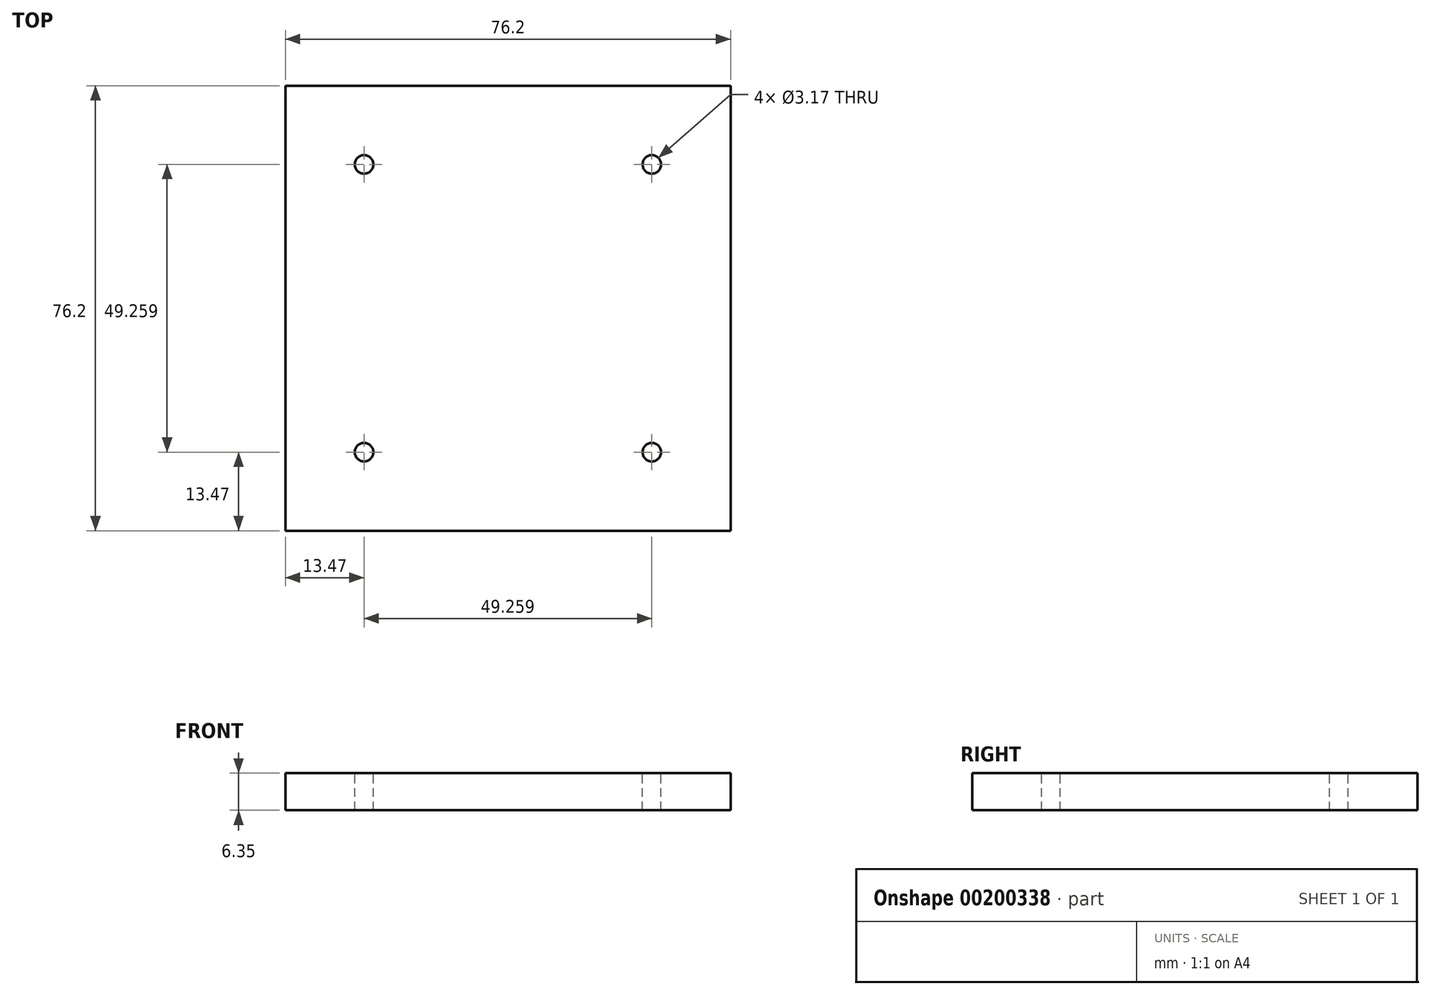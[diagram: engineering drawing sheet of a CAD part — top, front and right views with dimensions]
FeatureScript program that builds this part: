
annotation { "Feature Type Name" : "Feature", "Feature Type Description" : "" }
export const myFeature = defineFeature(function(context is Context, id is Id, definition is map)
    precondition{}
    {
        {
            var Q0;
            Q0=qCreatedBy(makeId("Top.planeOp"),FACE);
            var sketch = newSketch(context, id + "F0", { "sketchPlane" : qUnion([Q0])});
            skLineSegment(sketch, "E0.bottom", {"start": v(38.1, -38.1) * mm, "end": v(-38.1, -38.1) * mm});
            skLineSegment(sketch, "E0.top", {"start": v(38.1, 38.1) * mm, "end": v(-38.1, 38.1) * mm});
            skLineSegment(sketch, "E0.left", {"start": v(38.1, -38.1) * mm, "end": v(38.1, 38.1) * mm});
            skLineSegment(sketch, "E0.right", {"start": v(-38.1, -38.1) * mm, "end": v(-38.1, 38.1) * mm});
            skPoint(sketch, "E0.middle", {"position": v(0, 0) * mm});
            skSolve(sketch);
        }
        {
            var Q0;
            Q0=makeQuery(id+"F0.imprint","IMPRINT",FACE,{"disambiguationData":[TD([[makeQuery(id+"F0.imprint","IMPRINT",EDGE,{"derivedFrom":sQuery(id+"F0.wireOp",EDGE,"E0.bottom")}),-1.0]])]});
            extrude(context, id + "F1", {"entities" : qUnion([Q0]), "depth" : 6.35 * mm});
        }
        {
            var Q0;
            Q0=makeQuery(id+"F1.opExtrude","CAP_FACE",FACE,{"disambiguationData":[OSD([sQuery(id+"F0.wireOp",EDGE,"E0.bottom"),sQuery(id+"F0.wireOp",EDGE,"E0.top"),sQuery(id+"F0.wireOp",EDGE,"E0.left"),sQuery(id+"F0.wireOp",EDGE,"E0.right")])],"isStart":false});
            var sketch = newSketch(context, id + "F2", { "sketchPlane" : qUnion([Q0])});
            skLineSegment(sketch, "E1", {"start": v(-38.1, 38.1) * mm, "end": v(38.1, -38.1) * mm, "construction": true});
            skLineSegment(sketch, "E2", {"start": v(-38.1, -38.1) * mm, "end": v(38.1, 38.1) * mm, "construction": true});
            skLineSegment(sketch, "E3", {"start": v(-38.1, 0) * mm, "end": v(38.1, 0) * mm, "construction": true});
            skLineSegment(sketch, "E4", {"start": v(0, 38.1) * mm, "end": v(0, -38.1) * mm, "construction": true});
            skCircle(sketch, "E5", {"center": v(-24.63, 24.63) * mm, "radius": 1.59 * mm});
            skCircle(sketch, "E6.1.0", {"center": v(-24.63, -24.63) * mm, "radius": 1.59 * mm});
            skCircle(sketch, "E6.2.0", {"center": v(24.63, -24.63) * mm, "radius": 1.59 * mm});
            skCircle(sketch, "E6.3.0", {"center": v(24.63, 24.63) * mm, "radius": 1.59 * mm});
            skPoint(sketch, "E6.center", {"position": v(0, 0) * mm});
            skSolve(sketch);
        }
        {
            var Q0;
            Q0=qSketchRegion(id+"F2",true);
            extrude(context, id + "F3", {"entities" : qUnion([Q0]), "operationType" : NewBodyOperationType.REMOVE, "oppositeDirection" : true, "depth" : 25.4 * mm});
        }
    });
